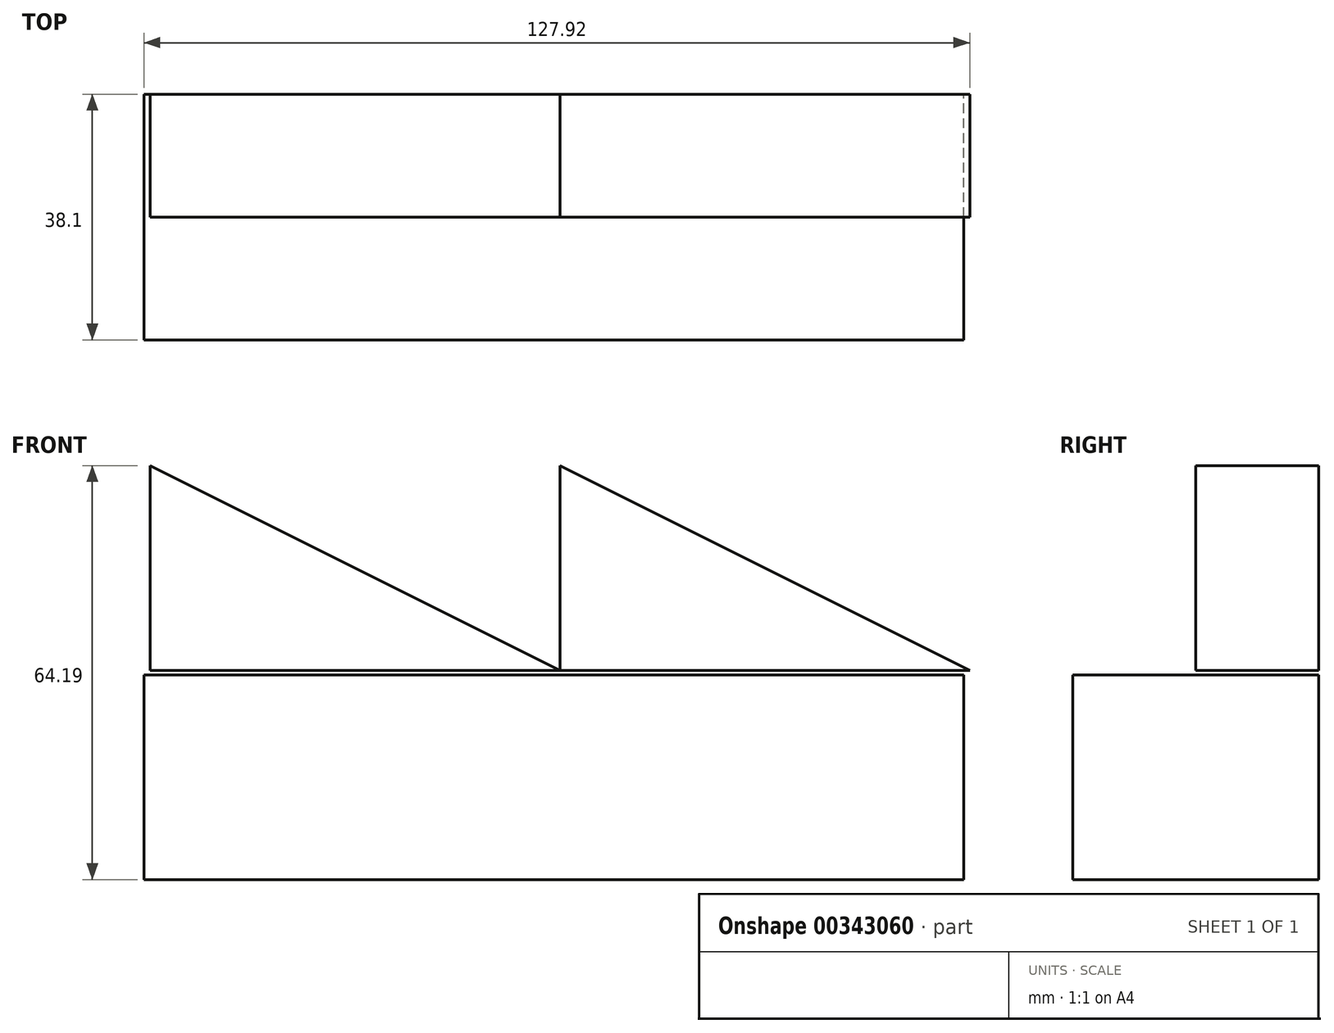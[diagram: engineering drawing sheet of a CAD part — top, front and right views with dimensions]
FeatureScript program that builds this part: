
annotation { "Feature Type Name" : "Feature", "Feature Type Description" : "" }
export const myFeature = defineFeature(function(context is Context, id is Id, definition is map)
    precondition{}
    {
        {
            var Q0;
            Q0=qCreatedBy(makeId("Front.planeOp"),FACE);
            var sketch = newSketch(context, id + "F0", { "sketchPlane" : qUnion([Q0])});
            skLineSegment(sketch, "E0", {"start": v(-67.87, -42.4) * mm, "end": v(59.13, -42.4) * mm});
            skLineSegment(sketch, "E1", {"start": v(-67.87, -42.4) * mm, "end": v(-67.87, -10.66) * mm});
            skLineSegment(sketch, "E2", {"start": v(-67.87, -10.66) * mm, "end": v(59.13, -10.66) * mm});
            skLineSegment(sketch, "E3", {"start": v(59.13, -10.66) * mm, "end": v(59.13, -42.4) * mm});
            skSolve(sketch);
        }
        {
            var Q0;
            Q0 = qSketchRegion(id + "F0", true);
            extrude(context, id + "F1", {"entities" : qUnion([Q0]), "depth" : 38.1 * mm});
        }
        {
            var Q0;
            Q0=qCreatedBy(makeId("Front.planeOp"),FACE);
            var sketch = newSketch(context, id + "F2", { "sketchPlane" : qUnion([Q0])});
            skLineSegment(sketch, "E4", {"start": v(-66.95, -9.97) * mm, "end": v(-66.95, 21.78) * mm});
            skLineSegment(sketch, "E5", {"start": v(-66.95, -9.97) * mm, "end": v(-3.45, -9.97) * mm});
            skLineSegment(sketch, "E6", {"start": v(-66.95, 21.78) * mm, "end": v(-3.45, -9.97) * mm});
            skLineSegment(sketch, "E7", {"start": v(-3.45, -9.97) * mm, "end": v(-3.45, 21.78) * mm});
            skLineSegment(sketch, "E8", {"start": v(-3.45, -9.97) * mm, "end": v(60.05, -9.97) * mm});
            skLineSegment(sketch, "E9", {"start": v(-3.45, 21.78) * mm, "end": v(60.05, -9.97) * mm});
            skSolve(sketch);
        }
        {
            var Q0;
            Q0 = qSketchRegion(id + "F2", true);
            extrude(context, id + "F3", {"entities" : qUnion([Q0]), "depth" : 19.05 * mm});
        }
    });
